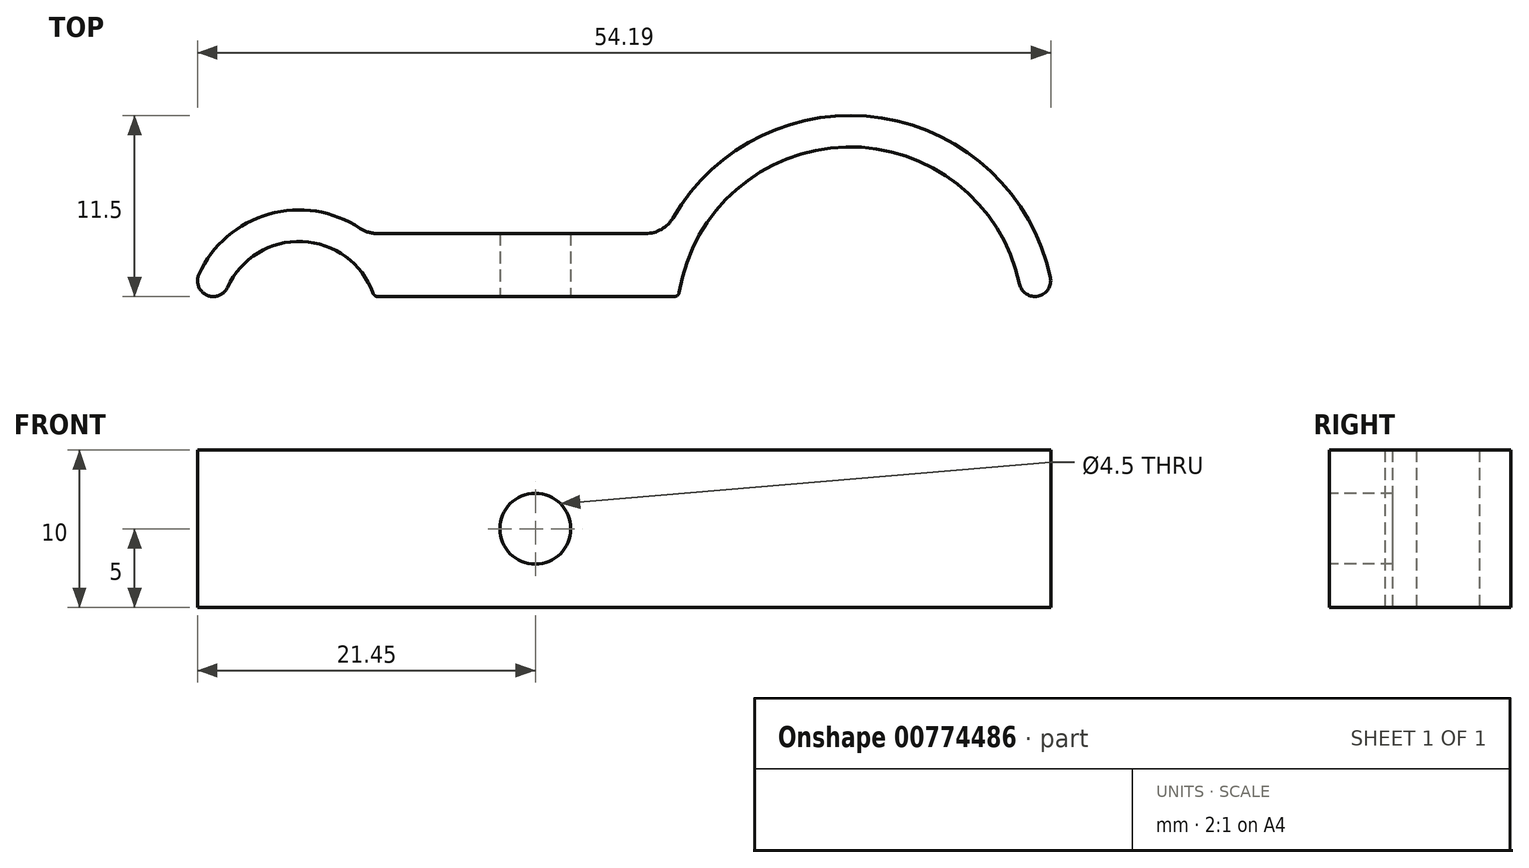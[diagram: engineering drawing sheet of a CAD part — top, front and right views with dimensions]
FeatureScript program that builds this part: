
annotation { "Feature Type Name" : "Feature", "Feature Type Description" : "" }
export const myFeature = defineFeature(function(context is Context, id is Id, definition is map)
    precondition{}
    {
        {
            var Q0;
            Q0=qCreatedBy(makeId("Top.planeOp"),FACE);
            var sketch = newSketch(context, id + "F0", { "sketchPlane" : qUnion([Q0])});
            skArc(sketch, "E0", {"start": v(4.7, 1.7) * mm, "mid": v(0.2, 5) * mm, "end": v(-4.55, 2.08) * mm});
            skArc(sketch, "E1", {"start": v(3.87, 5.83) * mm, "mid": v(-1.92, 6.73) * mm, "end": v(-6.36, 2.92) * mm});
            skArc(sketch, "E2", {"start": v(45.76, 2.3) * mm, "mid": v(34.73, 11) * mm, "end": v(24.14, 1.76) * mm});
            skArc(sketch, "E3", {"start": v(47.71, 2.7) * mm, "mid": v(37.03, 12.84) * mm, "end": v(23.74, 6.5) * mm});
            skLineSegment(sketch, "E4.0", {"start": v(-5.45, 1.5) * mm, "end": v(-5.45, 1.5) * mm});
            skLineSegment(sketch, "E5.0", {"start": v(4.97, 5.5) * mm, "end": v(22, 5.5) * mm});
            skPoint(sketch, "E6.orphan", {"position": v(-7, 0) * mm});
            skLineSegment(sketch, "E7.trimOffspring", {"start": v(5, 1.5) * mm, "end": v(23.84, 1.5) * mm});
            skLineSegment(sketch, "E8.trimOffspring", {"start": v(46.74, 1.5) * mm, "end": v(46.74, 1.5) * mm});
            skPoint(sketch, "E9.visualSharp", {"position": v(4.33, 5.5) * mm});
            skArc(sketch, "E9.filletArc", {"start": v(3.87, 5.83) * mm, "mid": v(4.4, 5.59) * mm, "end": v(4.97, 5.5) * mm});
            skPoint(sketch, "E10.visualSharp", {"position": v(23.22, 5.5) * mm});
            skArc(sketch, "E10.filletArc", {"start": v(22, 5.5) * mm, "mid": v(23, 5.77) * mm, "end": v(23.74, 6.5) * mm});
            skPoint(sketch, "E11.visualSharp", {"position": v(45.9, 1.5) * mm});
            skArc(sketch, "E11.filletArc", {"start": v(45.76, 2.3) * mm, "mid": v(46.1, 1.72) * mm, "end": v(46.74, 1.5) * mm});
            skPoint(sketch, "E12.visualSharp", {"position": v(47.91, 1.5) * mm});
            skArc(sketch, "E12.filletArc", {"start": v(46.74, 1.5) * mm, "mid": v(47.51, 1.87) * mm, "end": v(47.71, 2.7) * mm});
            skPoint(sketch, "E13.visualSharp", {"position": v(24.1, 1.5) * mm});
            skArc(sketch, "E13.filletArc", {"start": v(23.84, 1.5) * mm, "mid": v(24.04, 1.57) * mm, "end": v(24.14, 1.76) * mm});
            skPoint(sketch, "E14.visualSharp", {"position": v(4.77, 1.5) * mm});
            skArc(sketch, "E14.filletArc", {"start": v(4.7, 1.7) * mm, "mid": v(4.81, 1.56) * mm, "end": v(5, 1.5) * mm});
            skPoint(sketch, "E15.visualSharp", {"position": v(-4.77, 1.5) * mm});
            skArc(sketch, "E15.filletArc", {"start": v(-5.45, 1.5) * mm, "mid": v(-4.91, 1.66) * mm, "end": v(-4.55, 2.08) * mm});
            skPoint(sketch, "E16.visualSharp", {"position": v(-6.84, 1.5) * mm});
            skArc(sketch, "E16.filletArc", {"start": v(-6.36, 2.92) * mm, "mid": v(-6.3, 1.96) * mm, "end": v(-5.45, 1.5) * mm});
            skSolve(sketch);
        }
        {
            var Q0;
            Q0=makeQuery(id+"F0.imprint","IMPRINT",FACE,{"disambiguationData":[TD([[makeQuery(id+"F0.imprint","IMPRINT",EDGE,{"derivedFrom":sQuery(id+"F0.wireOp",EDGE,"E0")}),-1.0]])]});
            extrude(context, id + "F1", {"entities" : qUnion([Q0]), "depth" : (10) * mm, "offsetDistance" : 25 * mm});
        }
        {
            var Q0;
            Q0=makeQuery(id+"F1.opExtrude","SWEPT_FACE",FACE,{"disambiguationData":[OSD([sQuery(id+"F0.wireOp",EDGE,"E7.trimOffspring")])]});
            var sketch = newSketch(context, id + "F2", { "sketchPlane" : qUnion([Q0])});
            skCircle(sketch, "E17", {"center": v(15, 5) * mm, "radius": 2.25 * mm});
            skSolve(sketch);
        }
        {
            var Q0;
            Q0=makeQuery(id+"F2.imprint","IMPRINT",FACE,{"disambiguationData":[TD([[makeQuery(id+"F2.imprint","IMPRINT",EDGE,{"derivedFrom":sQuery(id+"F2.wireOp",EDGE,"E17")}),1.0]])]});
            extrude(context, id + "F3", {"entities" : qUnion([Q0]), "operationType" : NewBodyOperationType.REMOVE, "oppositeDirection" : true, "depth" : 25 * mm, "offsetDistance" : 25 * mm});
        }
    });
